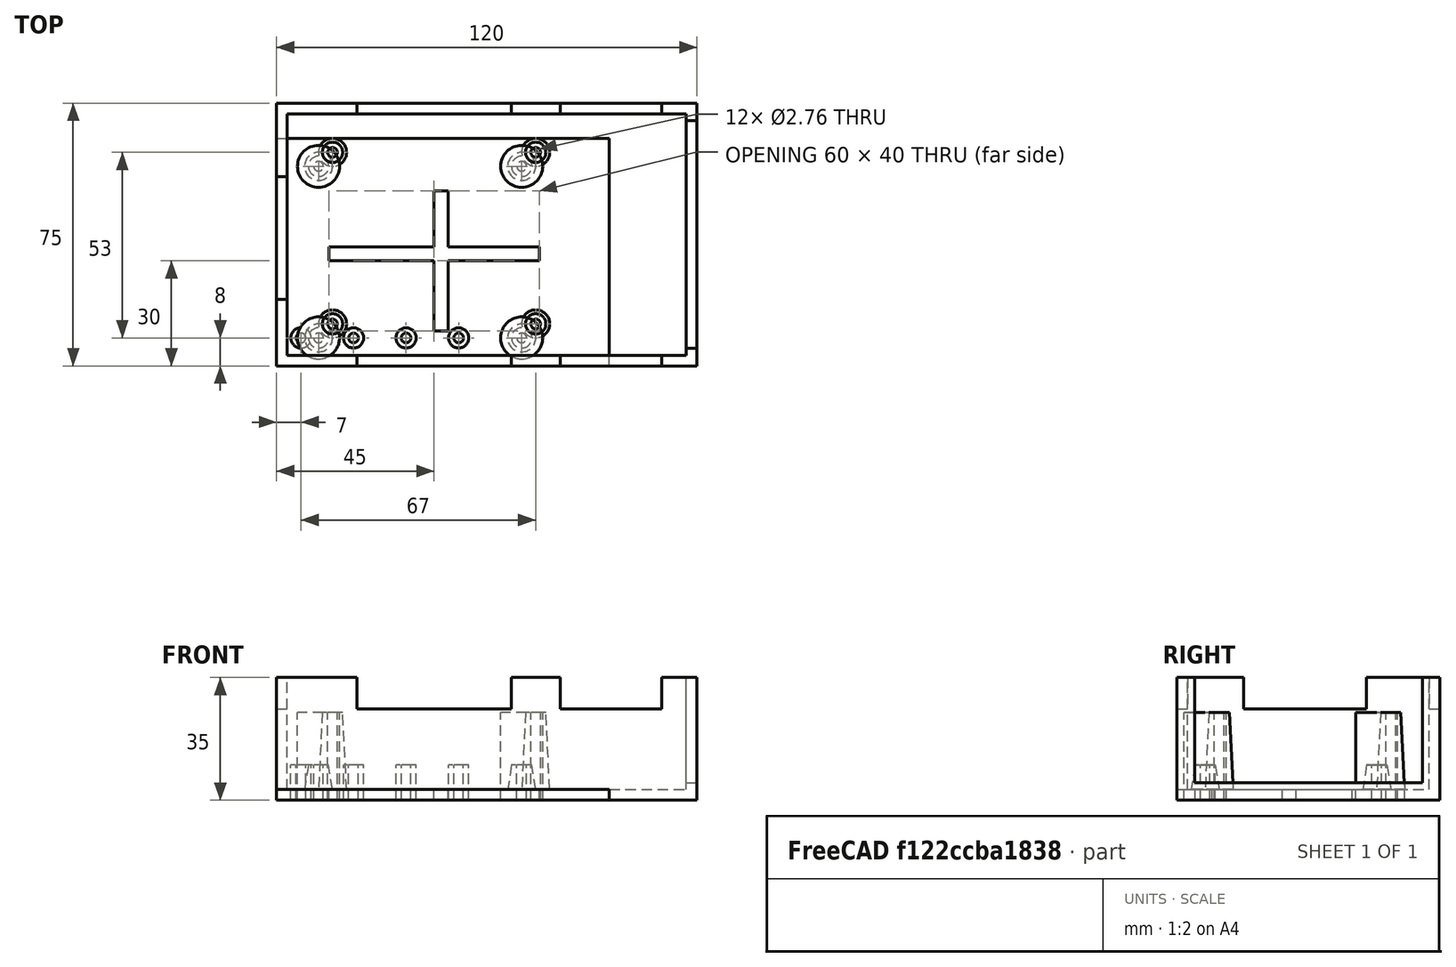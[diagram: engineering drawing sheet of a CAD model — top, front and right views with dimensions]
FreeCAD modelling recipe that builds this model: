
FCSTD DOCUMENT  (FreeCAD 0.16R6707 (Git))
Label: Raspberry
License: All rights reserved
LicenseURL: http://en.wikipedia.org/wiki/All_rights_reserved
objects: Part::Cylinder×20, Part::MultiFuse×11, Part::Box×10, Part::Cut×5, Part::Cone×4, Mesh::Feature×3, App::DocumentObjectGroup×3, Spreadsheet::Sheet×1
note: 50 computed .brp shape members not serialized (recipe doc carries the construction recipe); baked Part::Feature solids carry a one-line shape summary decoded from their .brp

FEATURE [Part::Cylinder] Cylinder  label="Zylinder 12/8"
  Angle = 360
  Height = 20
  Placement = pos=(12,8,-5) rot=(0,0,1;0rad)
  Radius = 1.38
FEATURE [Part::Cylinder] Cylinder001  label="Zylinder 70/57"
  Angle = 360
  Height = 20
  Placement = pos=(70,57,-5) rot=(0,0,1;0rad)
  Radius = 1.38
FEATURE [Part::Cylinder] Cylinder002  label="Zylinder 70/8"
  Angle = 360
  Height = 20
  Placement = pos=(70,8,-5) rot=(0,0,1;0rad)
  Radius = 1.38
FEATURE [Part::Cylinder] Cylinder003  label="Zylinder 12/57"
  Angle = 360
  Height = 20
  Placement = pos=(12,57,-5) rot=(0,0,1;0rad)
  Radius = 1.38
FEATURE [Part::MultiFuse] Fusion001  label="Schraubenlöcher"
  Shapes = -> [Cylinder003,Cylinder,Cylinder002,Cylinder001]
FEATURE [Part::Box] Box001  label="Extraktionsslot quer"
  Height = 5
  Length = 4
  Placement = pos=(45,10,0) rot=(0,0,1;0rad)
  Width = 40
FEATURE [Part::Box] Box002  label="Extraktionsslot hoch"
  Height = 5
  Length = 60
  Placement = pos=(15,30,0) rot=(0,0,1;0rad)
  Width = 4
FEATURE [Part::MultiFuse] Fusion  label="Extraktinosslots"
  Placement = pos=(0,0,-1) rot=(0,0,1;0rad)
  Shapes = -> [Box001,Box002]
FEATURE [Part::Cylinder] Cylinder008  label="Zylinder009"
  Angle = 360
  Height = 10
  Placement = pos=(7,8,0) rot=(0,0,1;0rad)
  Radius = 2.9
FEATURE [Part::Cylinder] Cylinder009  label="Zylinder001"
  Angle = 360
  Height = 10
  Placement = pos=(22,8,0) rot=(0,0,1;0rad)
  Radius = 2.9
FEATURE [Part::Cylinder] Cylinder010  label="Zylinder002"
  Angle = 360
  Height = 10
  Placement = pos=(37,8,0) rot=(0,0,1;0rad)
  Radius = 2.9
FEATURE [Part::Cylinder] Cylinder011  label="Zylinder003"
  Angle = 360
  Height = 10
  Placement = pos=(52,8,0) rot=(0,0,1;0rad)
  Radius = 2.9
FEATURE [Part::Cylinder] Cylinder012  label="Zylinder004"
  Angle = 360
  Height = 15
  Placement = pos=(7,8,-2) rot=(0,0,1;0rad)
  Radius = 1.38
FEATURE [Part::Cylinder] Cylinder013  label="Zylinder005"
  Angle = 360
  Height = 15
  Placement = pos=(22,8,-2) rot=(0,0,1;0rad)
  Radius = 1.38
FEATURE [Part::Cylinder] Cylinder014  label="Zylinder006"
  Angle = 360
  Height = 15
  Placement = pos=(37,8,-2) rot=(0,0,1;0rad)
  Radius = 1.38
FEATURE [Part::Cylinder] Cylinder015  label="Zylinder007"
  Angle = 360
  Height = 15
  Placement = pos=(52,8,-2) rot=(0,0,1;0rad)
  Radius = 1.38
FEATURE [Part::Box] Box004  label="Würfel"
  Height = 35
  Length = 120
  Width = 75
FEATURE [Part::Box] Box005  label="Würfel001"
  Height = 35
  Length = 114
  Placement = pos=(3,3,3) rot=(0,0,1;0rad)
  Width = 69
FEATURE [Part::Cylinder] Cylinder016  label="Zylinder12/57"
  Angle = 360
  Height = 25
  Placement = pos=(12,57,0) rot=(0,0,1;0rad)
  Radius = 6
FEATURE [Part::Cylinder] Cylinder017  label="Zylinder12/08"
  Angle = 360
  Height = 25
  Placement = pos=(12,8,0) rot=(0,0,1;0rad)
  Radius = 6
FEATURE [Part::Cylinder] Cylinder018  label="Zylinder70/57"
  Angle = 360
  Height = 25
  Placement = pos=(70,57,0) rot=(0,0,1;0rad)
  Radius = 6
FEATURE [Part::Cylinder] Cylinder019  label="Zylinder70/08"
  Angle = 360
  Height = 25
  Placement = pos=(70,8,0) rot=(0,0,1;0rad)
  Radius = 6
FEATURE [Part::MultiFuse] Fusion007  label="Distanzhalter001"
  Shapes = -> [Cylinder019,Cylinder018,Cylinder017,Cylinder016]
FEATURE [Part::Cylinder] Cylinder020  label="Zylinder70/058"
  Angle = 360
  Height = 30
  Placement = pos=(74,12,-2) rot=(0,0,1;0rad)
  Radius = 1.38
FEATURE [Part::Cylinder] Cylinder021  label="Zylinder70/059"
  Angle = 360
  Height = 30
  Placement = pos=(16,12,-2) rot=(0,0,1;0rad)
  Radius = 1.38
FEATURE [Part::Cylinder] Cylinder022  label="Zylinder70/060"
  Angle = 360
  Height = 30
  Placement = pos=(16,61,-2) rot=(0,0,1;0rad)
  Radius = 1.38
FEATURE [Part::Cylinder] Cylinder023  label="Zylinder70/061"
  Angle = 360
  Height = 30
  Placement = pos=(74,61,-2) rot=(0,0,1;0rad)
  Radius = 1.38
FEATURE [Part::MultiFuse] Fusion008
  Shapes = -> [Cylinder020,Cylinder023,Cylinder022,Cylinder021]
FEATURE [Part::Box] Box006  label="RJ45_USB_Cutout"
  Height = 35
  Length = 10
  Placement = pos=(115,5,5) rot=(0,0,1;0rad)
  Width = 65
FEATURE [Part::Box] Box007  label="Würfel002"
  Height = 10
  Length = 44
  Placement = pos=(23,-10,26) rot=(0,0,1;0rad)
  Width = 20
FEATURE [Part::Box] Box008  label="Würfel003"
  Height = 10
  Length = 44
  Placement = pos=(23,68,26) rot=(0,0,1;0rad)
  Width = 20
FEATURE [Part::Box] Box009  label="Würfel004"
  Height = 10
  Length = 29
  Placement = pos=(81,-10,26) rot=(0,0,1;0rad)
  Width = 20
FEATURE [Part::Box] Box010  label="Würfel005"
  Height = 10
  Length = 29
  Placement = pos=(81,60,26) rot=(0,0,1;0rad)
  Width = 20
FEATURE [Part::Box] Box011  label="Würfel006"
  Height = 10
  Length = 20
  Placement = pos=(-10,19,26) rot=(0,0,1;0rad)
  Width = 35
FEATURE [Part::MultiFuse] Fusion010
  Shapes = -> [Box007,Box011,Box010,Box009,Box008]
FEATURE [Part::MultiFuse] Fusion011
  Shapes = -> [Cylinder012,Cylinder013,Cylinder014,Cylinder015]
FEATURE [Part::MultiFuse] Fusion012
  Shapes = -> [Cylinder010,Cylinder008,Cylinder009,Cylinder011]
FEATURE [Part::Cut] Cut005  label="Distanzen"
  Base = -> Fusion012
  Tool = -> Fusion011
FEATURE [Mesh::Feature] Mesh  label="Distanzen (Meshed)"
FEATURE [App::DocumentObjectGroup] Gruppe  label="Distanzhalter"
  Group = -> [Cut005,Mesh]
FEATURE [Part::MultiFuse] Fusion013
  Shapes = -> [Fusion,Fusion001]
FEATURE [Part::Cut] Cut  label="Bodenplatte"
  Tool = -> Fusion013
FEATURE [Mesh::Feature] Mesh001  label="Bodenplatte (Meshed)"
FEATURE [App::DocumentObjectGroup] Gruppe002  label="Boden"
  Group = -> [Cut,Mesh001]
FEATURE [Part::MultiFuse] Fusion014
  Shapes = -> [Fusion010,Box006]
FEATURE [Part::Cone] Cone  label="Kegel"
  Angle = 360
  Height = 22
  Placement = pos=(74,12,3) rot=(0,0,1;0rad)
  Radius1 = 4
  Radius2 = 2.9
FEATURE [Part::Cone] Cone001  label="Kegel001"
  Angle = 360
  Height = 22
  Placement = pos=(74,61,3) rot=(0,0,1;0rad)
  Radius1 = 4
  Radius2 = 2.9
FEATURE [Part::Cone] Cone002  label="Kegel002"
  Angle = 360
  Height = 22
  Placement = pos=(16,12,3) rot=(0,0,1;0rad)
  Radius1 = 4
  Radius2 = 2.9
FEATURE [Part::Cone] Cone003  label="Kegel003"
  Angle = 360
  Height = 22
  Placement = pos=(16,61,3) rot=(0,0,1;0rad)
  Radius1 = 4
  Radius2 = 2.9
FEATURE [Part::MultiFuse] Fusion015
  Shapes = -> [Cone,Cone003,Cone002,Cone001]
FEATURE [Spreadsheet::Sheet] Spreadsheet
  cells = A1=Bodenplatte; B1=l; C1=b; D1=h; B2=95; C2=65; D2=3
FEATURE [Part::Cut] Cut006
  Base = -> Box004
  Tool = -> Box005
FEATURE [Part::Cut] Cut007
  Base = -> Cut006
  Tool = -> Fusion014
FEATURE [Part::MultiFuse] Fusion016
  Shapes = -> [Cut007,Fusion015]
FEATURE [Part::Cut] Cut008  label="Deckelkonstruktion"
  Base = -> Fusion016
  Tool = -> Fusion008
FEATURE [Mesh::Feature] Mesh002  label="Deckelkonstruktion (Meshed)"
FEATURE [App::DocumentObjectGroup] Gruppe001  label="Deckel"
  Group = -> [Cut008,Mesh002]
